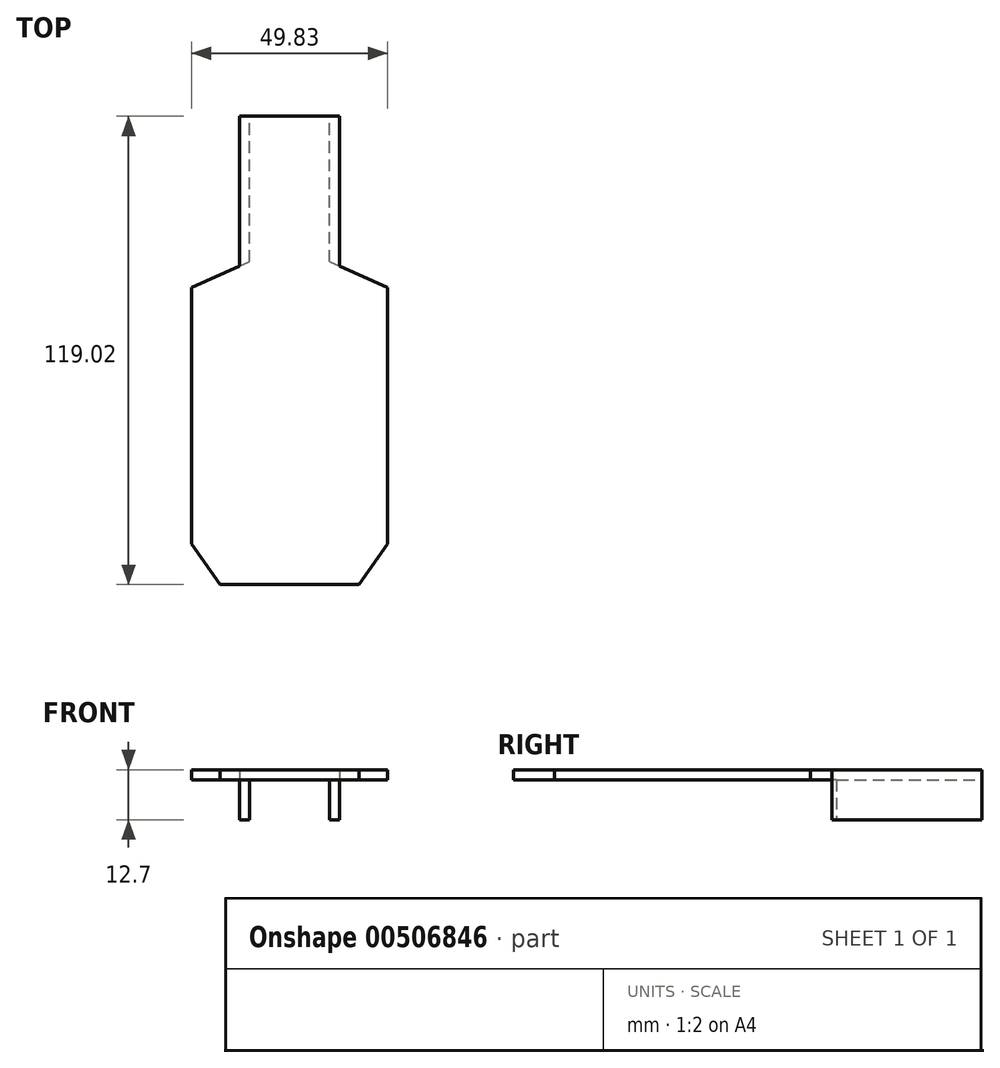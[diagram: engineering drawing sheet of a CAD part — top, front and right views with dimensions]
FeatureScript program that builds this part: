
annotation { "Feature Type Name" : "Feature", "Feature Type Description" : "" }
export const myFeature = defineFeature(function(context is Context, id is Id, definition is map)
    precondition{}
    {
        {
            var Q0;
            Q0=qCreatedBy(makeId("Top.planeOp"),FACE);
            var sketch = newSketch(context, id + "F0", { "sketchPlane" : qUnion([Q0])});
            skLineSegment(sketch, "E0", {"start": v(-4.93, 47.68) * mm, "end": v(7.28, 42.24) * mm});
            skLineSegment(sketch, "E1", {"start": v(7.28, 42.24) * mm, "end": v(7.28, -22.84) * mm});
            skLineSegment(sketch, "E2", {"start": v(7.28, -22.84) * mm, "end": v(0, -33.24) * mm});
            skLineSegment(sketch, "E3", {"start": v(0, -33.24) * mm, "end": v(-35.27, -33.24) * mm});
            skLineSegment(sketch, "E4", {"start": v(-35.27, -33.24) * mm, "end": v(-42.55, -22.84) * mm});
            skLineSegment(sketch, "E5", {"start": v(-42.55, -22.84) * mm, "end": v(-42.55, 42.24) * mm});
            skLineSegment(sketch, "E6", {"start": v(-42.55, 42.24) * mm, "end": v(-30.33, 47.68) * mm});
            skPoint(sketch, "E7", {"position": v(-23.98, 38.72) * mm});
            skPoint(sketch, "E8", {"position": v(-11.28, 38.72) * mm});
            skPoint(sketch, "E9", {"position": v(0, 38.72) * mm});
            skLineSegment(sketch, "E10", {"start": v(-30.33, 47.68) * mm, "end": v(-4.93, 47.68) * mm});
            skLineSegment(sketch, "E11.top", {"start": v(-30.33, 85.78) * mm, "end": v(-4.93, 85.78) * mm});
            skLineSegment(sketch, "E11.left", {"start": v(-30.33, 47.68) * mm, "end": v(-30.33, 85.78) * mm});
            skLineSegment(sketch, "E11.right", {"start": v(-4.93, 47.68) * mm, "end": v(-4.93, 85.78) * mm});
            skSolve(sketch);
        }
        {
            var Q0;
            Q0=makeQuery(id+"F0.imprint","IMPRINT",FACE,{"disambiguationData":[TD([[makeQuery(id+"F0.imprint","IMPRINT",EDGE,{"derivedFrom":sQuery(id+"F0.wireOp",EDGE,"r2QPg50F-n5vq-uU06-EfIU-YvwZcXLQOVtD")}),-1.0]])]});
            var Q1;
            Q1=makeQuery(id+"F0.imprint","IMPRINT",FACE,{"disambiguationData":[TD([[makeQuery(id+"F0.imprint","IMPRINT",EDGE,{"derivedFrom":sQuery(id+"F0.wireOp",EDGE,"E0")}),-1.0]])]});
            var Q2;
            Q2=makeQuery(id+"F0.imprint","IMPRINT",FACE,{"disambiguationData":[TD([[makeQuery(id+"F0.imprint","IMPRINT",EDGE,{"derivedFrom":sQuery(id+"F0.wireOp",EDGE,"E10")}),1.0]])]});
            extrude(context, id + "F1", {"entities" : qUnion([Q0, Q1, Q2]), "depth" : 12.7 * mm, "offsetDistance" : 25.4 * mm});
        }
        {
            var Q0;
            Q0=makeQuery(id+"F1.opExtrude","SWEPT_FACE",FACE,{"disambiguationData":[OSD([sQuery(id+"F0.wireOp",EDGE,"E1")])]});
            var Q1;
            Q1=makeQuery(id+"F1.opExtrude","SWEPT_FACE",FACE,{"disambiguationData":[OSD([sQuery(id+"F0.wireOp",EDGE,"E0")])]});
            var Q2;
            Q2=makeQuery(id+"F1.opExtrude","SWEPT_FACE",FACE,{"disambiguationData":[OSD([sQuery(id+"F0.wireOp",EDGE,"E2")])]});
            var Q3;
            Q3=makeQuery(id+"F1.opExtrude","SWEPT_FACE",FACE,{"disambiguationData":[OSD([sQuery(id+"F0.wireOp",EDGE,"E6")])]});
            var Q4;
            Q4=makeQuery(id+"F1.opExtrude","CAP_FACE",FACE,{"disambiguationData":[OSD([sQuery(id+"F0.wireOp",EDGE,"E0"),sQuery(id+"F0.wireOp",EDGE,"E1"),sQuery(id+"F0.wireOp",EDGE,"E2"),sQuery(id+"F0.wireOp",EDGE,"E3"),sQuery(id+"F0.wireOp",EDGE,"E4"),sQuery(id+"F0.wireOp",EDGE,"E5"),sQuery(id+"F0.wireOp",EDGE,"E6"),sQuery(id+"F0.wireOp",EDGE,"E11.top"),sQuery(id+"F0.wireOp",EDGE,"E11.left"),sQuery(id+"F0.wireOp",EDGE,"E11.right")])],"isStart":true});
            var Q5;
            Q5=makeQuery(id+"F1.opExtrude","SWEPT_FACE",FACE,{"disambiguationData":[OSD([sQuery(id+"F0.wireOp",EDGE,"E5")])]});
            var Q6;
            Q6=makeQuery(id+"F1.opExtrude","SWEPT_FACE",FACE,{"disambiguationData":[OSD([sQuery(id+"F0.wireOp",EDGE,"E3")])]});
            var Q7;
            Q7=makeQuery(id+"F1.opExtrude","SWEPT_FACE",FACE,{"disambiguationData":[OSD([sQuery(id+"F0.wireOp",EDGE,"E4")])]});
            var Q8;
            Q8=makeQuery(id+"F1.opExtrude","SWEPT_FACE",FACE,{"disambiguationData":[OSD([sQuery(id+"F0.wireOp",EDGE,"E11.top")])]});
            shell(context, id + "F2", {"entities" : qUnion([Q0, Q1, Q2, Q3, Q4, Q5, Q6, Q7, Q8]), "thickness" : 2.54 * mm});
        }
    });
